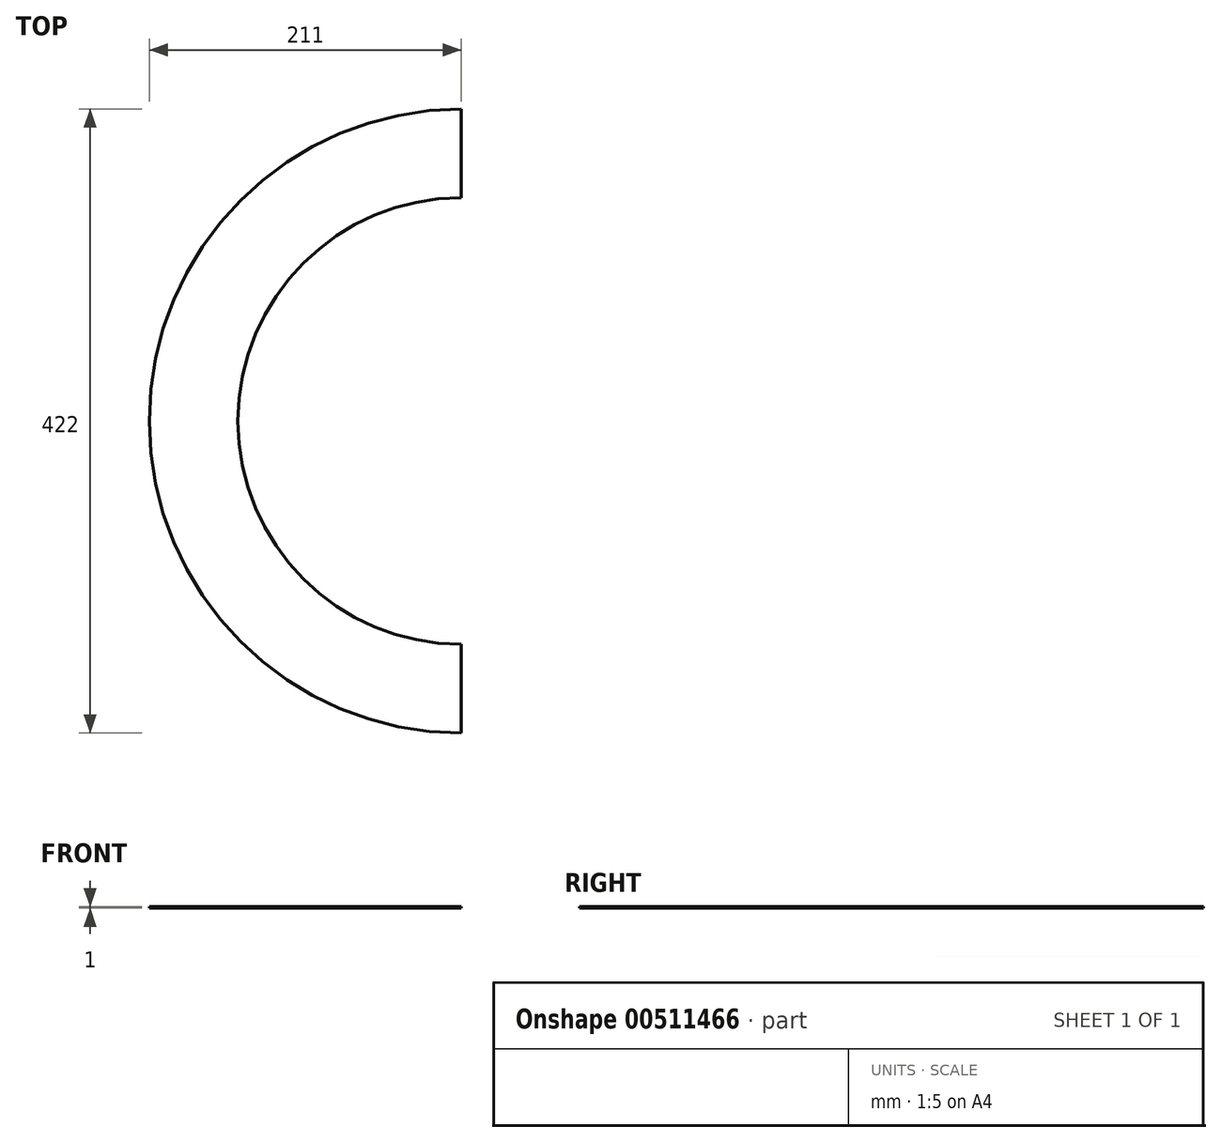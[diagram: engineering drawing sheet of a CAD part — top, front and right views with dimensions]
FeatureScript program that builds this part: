
annotation { "Feature Type Name" : "Feature", "Feature Type Description" : "" }
export const myFeature = defineFeature(function(context is Context, id is Id, definition is map)
    precondition{}
    {
        {
            var Q0;
            Q0=qCreatedBy(makeId("Top.planeOp"),FACE);
            var sketch = newSketch(context, id + "F0", { "sketchPlane" : qUnion([Q0])});
            skArc(sketch, "E0", {"start": v(0, 211) * mm, "mid": v(-211, 0) * mm, "end": v(0, -211) * mm});
            skArc(sketch, "E1", {"start": v(0, 151) * mm, "mid": v(-151, 0) * mm, "end": v(0, -151) * mm});
            skLineSegment(sketch, "E2", {"start": v(0, -211) * mm, "end": v(0, -151) * mm});
            skLineSegment(sketch, "E3.trimOffspring", {"start": v(0, 151) * mm, "end": v(0, 211) * mm});
            skSolve(sketch);
        }
        {
            var Q0;
            Q0=makeQuery(id+"F0.imprint","IMPRINT",FACE,{"disambiguationData":[TD([[makeQuery(id+"F0.imprint","IMPRINT",EDGE,{"derivedFrom":sQuery(id+"F0.wireOp",EDGE,"E0")}),1.0]])]});
            extrude(context, id + "F1", {"entities" : qUnion([Q0]), "oppositeDirection" : true, "depth" : 1 * mm});
        }
    });
